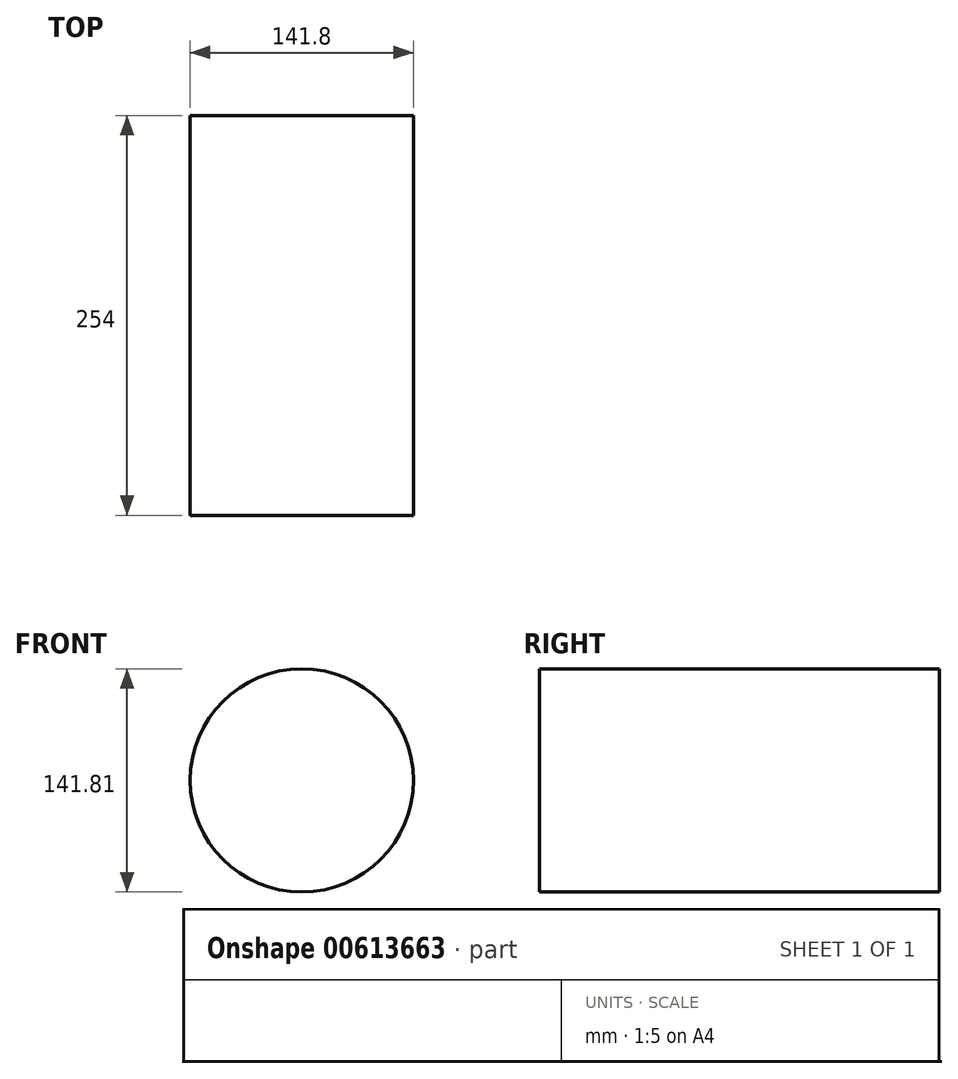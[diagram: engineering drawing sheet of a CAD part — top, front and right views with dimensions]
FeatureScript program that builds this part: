
annotation { "Feature Type Name" : "Feature", "Feature Type Description" : "" }
export const myFeature = defineFeature(function(context is Context, id is Id, definition is map)
    precondition{}
    {
        {
            var Q0;
            Q0=qCreatedBy(makeId("Front.planeOp"),FACE);
            var sketch = newSketch(context, id + "F0", { "sketchPlane" : qUnion([Q0])});
            skCircle(sketch, "E0", {"center": v(-61.1, 41.2) * mm, "radius": 70.9 * mm});
            skSolve(sketch);
        }
        {
            var Q0;
            Q0 = qSketchRegion(id + "F0", true);
            extrude(context, id + "F1", {"entities" : qUnion([Q0]), "oppositeDirection" : true, "depth" : 254 * mm, "offsetDistance" : 25.4 * mm});
        }
    });
